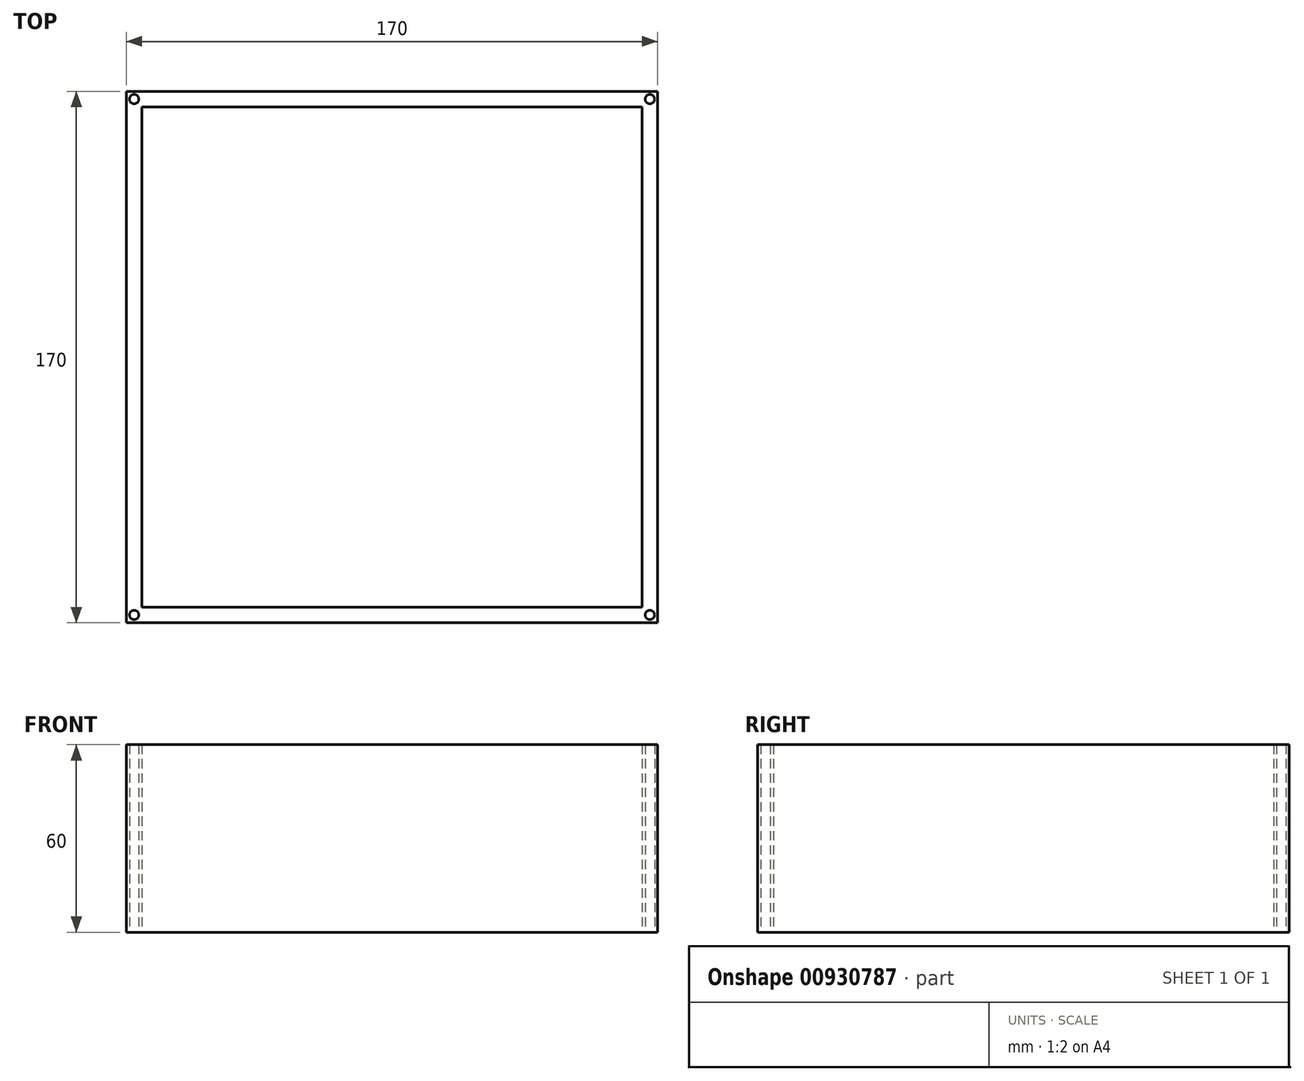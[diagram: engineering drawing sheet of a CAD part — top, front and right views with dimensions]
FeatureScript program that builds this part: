
annotation { "Feature Type Name" : "Feature", "Feature Type Description" : "" }
export const myFeature = defineFeature(function(context is Context, id is Id, definition is map)
    precondition{}
    {
        {
            var Q0;
            Q0=qCreatedBy(makeId("Top.planeOp"),FACE);
            var sketch = newSketch(context, id + "F0", { "sketchPlane" : qUnion([Q0])});
            skLineSegment(sketch, "E0.bottom", {"start": v(85, -85) * mm, "end": v(-85, -85) * mm});
            skLineSegment(sketch, "E0.top", {"start": v(85, 85) * mm, "end": v(-85, 85) * mm});
            skLineSegment(sketch, "E0.left", {"start": v(85, -85) * mm, "end": v(85, 85) * mm});
            skLineSegment(sketch, "E0.right", {"start": v(-85, -85) * mm, "end": v(-85, 85) * mm});
            skPoint(sketch, "E0.middle", {"position": v(0, 0) * mm});
            skLineSegment(sketch, "E1.0", {"start": v(80, 80) * mm, "end": v(-80, 80) * mm});
            skLineSegment(sketch, "E1.1", {"start": v(80, -80) * mm, "end": v(80, 80) * mm});
            skLineSegment(sketch, "E1.2", {"start": v(80, -80) * mm, "end": v(-80, -80) * mm});
            skLineSegment(sketch, "E1.3", {"start": v(-80, -80) * mm, "end": v(-80, 80) * mm});
            skLineSegment(sketch, "E2", {"start": v(-85, 85) * mm, "end": v(-80, 80) * mm});
            skCircle(sketch, "E3", {"center": v(-82.5, 82.5) * mm, "radius": 1.5 * mm});
            skLineSegment(sketch, "E4", {"start": v(80, 80) * mm, "end": v(85, 85) * mm});
            skCircle(sketch, "E5", {"center": v(82.5, 82.5) * mm, "radius": 1.5 * mm});
            skLineSegment(sketch, "E6", {"start": v(85, -85) * mm, "end": v(80, -80) * mm});
            skCircle(sketch, "E7", {"center": v(82.5, -82.5) * mm, "radius": 1.5 * mm});
            skLineSegment(sketch, "E8", {"start": v(-85, -85) * mm, "end": v(-80, -80) * mm});
            skCircle(sketch, "E9", {"center": v(-82.5, -82.5) * mm, "radius": 1.5 * mm});
            skSolve(sketch);
        }
        {
            var Q0;
            Q0=makeQuery(id+"F0.imprint","IMPRINT",FACE,{"disambiguationData":[TD([[makeQuery(id+"F0.imprint","IMPRINT",EDGE,{"derivedFrom":sQuery(id+"F0.wireOp",EDGE,"E0.bottom")}),-1.0]])]});
            var Q1;
            {var subQ4=sQuery(id+"F0.wireOp",EDGE,"E0.right");Q1=makeQuery(id+"F0.imprint","IMPRINT",FACE,{"disambiguationData":[TD([[makeQuery(id+"F0.imprint","IMPRINT",EDGE,{"derivedFrom":subQ4}),-1.0]])]});}
            var Q2;
            {var subQ1=sQuery(id+"F0.wireOp",EDGE,"E0.left");Q2=makeQuery(id+"F0.imprint","IMPRINT",FACE,{"disambiguationData":[TD([[makeQuery(id+"F0.imprint","IMPRINT",EDGE,{"derivedFrom":subQ1}),1.0]])]});}
            var Q3;
            {var subQ1=sQuery(id+"F0.wireOp",EDGE,"E0.top");Q3=makeQuery(id+"F0.imprint","IMPRINT",FACE,{"disambiguationData":[TD([[makeQuery(id+"F0.imprint","IMPRINT",EDGE,{"derivedFrom":subQ1}),1.0]])]});}
            extrude(context, id + "F1", {"entities" : qUnion([Q0, Q1, Q2, Q3]), "depth" : 60 * mm, "offsetDistance" : 25 * mm});
        }
    });
